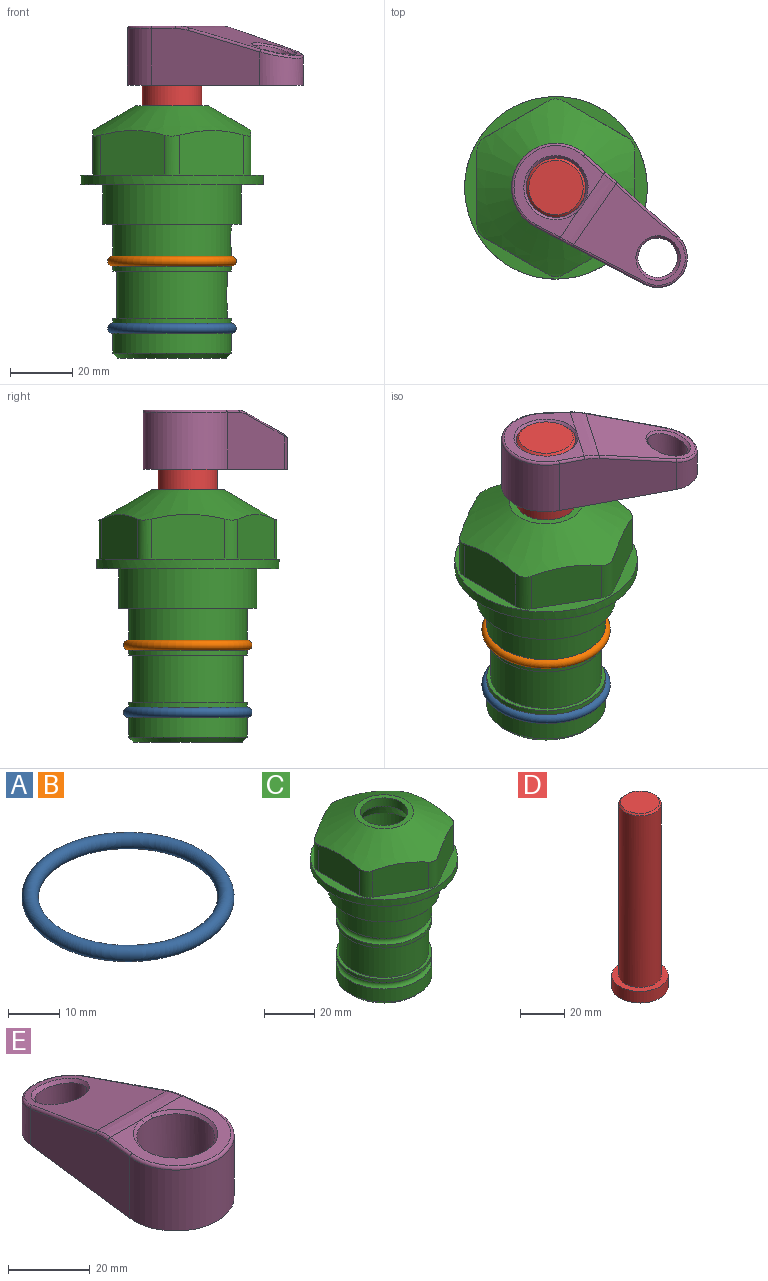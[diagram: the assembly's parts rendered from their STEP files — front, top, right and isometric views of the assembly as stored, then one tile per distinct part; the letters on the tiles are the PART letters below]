
ASSEMBLY  parts=5 mates=4
PART A: 1 faces, bbox 44.7x44.7x3.2 mm
  f0: torus R=19.05mm, axis (0,0,1), area 1193.9mm2
PART B: same geometry as A
PART C: 36 faces, bbox 58.7x58.7x81 mm
  f0: cylinder r=17.78mm len=35.56mm, axis (0,0,1), area 1670.8mm2, adj f23,f24,f31
  f1: cylinder r=19.05mm len=38.1mm, axis (0,0,1), area 1191.9mm2, adj f26,f27,f30
  f2: plane 58.66x58.66mm, normal (0,0,-1), area 1150.6mm2, adj f3,f28
  f3: cylinder r=29.33mm len=58.66mm, axis (0,0,-1), area 585.1mm2, adj f2,f4
  f4: plane 58.66x58.66mm, normal (0,0,1), area 475.9mm2, adj f3,f5,f6,f7,f8,f9,f10,f11
  f5: plane 20.32x14.34mm, normal (-0.5,0.87,0), area 324.4mm2, adj f4,f15,f16,f17
  f6: plane 20.32x14.34mm, normal (0.5,0.87,0), area 324.4mm2, adj f4,f14,f15,f17
  f7: plane 23.48x14.34mm, normal (1,0,0), area 324.4mm2, adj f4,f13,f14,f17
  f8: plane 20.32x14.34mm, normal (0.5,-0.87,0), area 324.4mm2, adj f4,f12,f13,f17
  f9: plane 20.32x14.34mm, normal (-0.5,-0.87,0), area 324.4mm2, adj f4,f11,f12,f17
  f10: plane 23.48x14.34mm, normal (-1,0,0), area 324.4mm2, adj f4,f11,f16,f17
  f11: cylinder r=5.08mm len=12.85mm, axis (0,0,-1), area 67.2mm2, adj f4,f9,f10,f17
  f12: cylinder r=5.08mm len=12.85mm, axis (0,0,-1), area 67.2mm2, adj f4,f8,f9,f17
  f13: cylinder r=5.08mm len=12.85mm, axis (0,0,-1), area 67.2mm2, adj f4,f7,f8,f17
  f14: cylinder r=5.08mm len=12.85mm, axis (0,0,-1), area 67.2mm2, adj f4,f6,f7,f17
  f15: cylinder r=5.08mm len=12.85mm, axis (0,0,-1), area 67.2mm2, adj f4,f5,f6,f17
  f16: cylinder r=5.08mm len=12.85mm, axis (0,0,-1), area 67.2mm2, adj f4,f5,f10,f17
  f17: cone r=11.73mm half-angle=60deg, axis (0,0,-1), area 2071.8mm2, adj f5,f6,f7,f8,f9,f10,f11,f12
  f18: plane 23.46x23.46mm, normal (0,0,1), area 147.4mm2, adj f17,f35
  f19: plane 34.93x34.93mm, normal (0,0,-1), area 958mm2, adj f29
  f20: cylinder r=19.05mm len=38.1mm, axis (0,0,1), area 760.1mm2, adj f21,f29
  f21: torus R=19.05mm, axis (0,0,1), area 565.3mm2, adj f20,f22
  f22: cylinder r=19.05mm len=38.1mm, axis (0,0,1), area 190mm2, adj f21,f23
  f23: plane 38.1x38.1mm, normal (0,0,1), area 146.9mm2, adj f0,f22
  f24: plane 38.1x38.1mm, normal (0,0,-1), area 146.9mm2, adj f0,f25
  f25: cylinder r=19.05mm len=38.1mm, axis (0,0,1), area 190mm2, adj f24,f26
  f26: torus R=19.05mm, axis (0,0,1), area 565.3mm2, adj f1,f25
  f27: plane 44.45x44.45mm, normal (0,0,-1), area 411.7mm2, adj f1,f28
  f28: cylinder r=22.23mm len=44.45mm, axis (0,0,1), area 1773.5mm2, adj f2,f27
  f29: cone r=19.05mm half-angle=45deg, axis (0,0,1), area 257.5mm2, adj f19,f20
  f30: cylinder r=3.17mm len=6.75mm, axis (-1,0,0), area 128mm2, adj f1,f33
  f31: cylinder r=3.17mm len=6.35mm, axis (-1,0,0), area 102.5mm2, adj f0,f33
  f32: plane 25.4x25.4mm, normal (0,0,1), area 506.7mm2, adj f33
  f33: cylinder r=12.7mm len=66.42mm, axis (0,0,-1), area 5236.2mm2, adj f30,f31,f32,f34
  f34: cone r=9.53mm half-angle=30deg, axis (0,0,-1), area 443.4mm2, adj f33,f35
  f35: cylinder r=9.53mm len=19.05mm, axis (0,0,-1), area 240.9mm2, adj f18,f34
PART D: 6 faces, bbox 25.4x25.4x101.6 mm
  f0: plane 17.46x17.46mm, normal (0,0,1), area 239.5mm2, adj f5
  f1: plane 25.4x25.4mm, normal (0,0,-1), area 506.7mm2, adj f2
  f2: cylinder r=12.7mm len=25.4mm, axis (0,0,1), area 506.7mm2, adj f1,f3
  f3: plane 25.4x25.4mm, normal (0,0,1), area 221.7mm2, adj f2,f4
  f4: cylinder r=9.53mm len=94.46mm, axis (0,0,1), area 5653mm2, adj f3,f5
  f5: cone r=8.73mm half-angle=45deg, axis (0,0,-1), area 64.4mm2, adj f0,f4
PART E: 31 faces, bbox 31.7x65.5x19.8 mm
  f0: plane 39.12x18.26mm, normal (0.99,0.12,0), area 612.2mm2, adj f1,f4,f7,f11,f13,f15
  f1: cylinder r=9.53mm len=18.91mm, axis (0,0,-1), area 296.1mm2, adj f0,f2,f7,f17
  f2: plane 39.12x18.26mm, normal (-0.99,0.12,0), area 612.2mm2, adj f1,f4,f7,f12,f14,f16
  f3: cylinder r=6.35mm len=12.7mm, axis (0,0,-1), area 362.4mm2, adj f7,f18
  f4: cylinder r=14.29mm len=28.58mm, axis (0,0,-1), area 882.2mm2, adj f0,f2,f7,f10
  f5: cylinder r=9.53mm len=19.05mm, axis (0,0,-1), area 1092.6mm2, adj f7,f19,f20
  f6: plane 26.99x23.69mm, normal (0,0,1), area 216.2mm2, adj f9,f10,f11,f12,f19
  f7: plane 63.5x28.58mm, normal (0,0,-1), area 661.8mm2, adj f0,f1,f2,f3,f4,f5,f22,f23
  f8: plane 33.52x23.6mm, normal (0,0.26,0.97), area 486mm2, adj f9,f15,f16,f17,f18
  f9: cylinder r=19.05mm len=24.72mm, axis (1,0,0), area 120.4mm2, adj f6,f8,f13,f14,f20
  f10: torus R=13.49mm, axis (0,0,1), area 59mm2, adj f4,f6,f11,f12
  f11: cylinder r=0.79mm len=8.67mm, axis (0.12,-0.99,0), area 10.8mm2, adj f0,f6,f10,f13
  f12: cylinder r=0.79mm len=8.67mm, axis (0.12,0.99,0), area 10.8mm2, adj f2,f6,f10,f14
  f13: bspline ~4.95x1.42mm, area 6.1mm2, adj f0,f9,f11,f15
  f14: bspline ~4.95x1.42mm, area 6.1mm2, adj f2,f9,f12,f16
  f15: cylinder r=0.79mm len=25.95mm, axis (0.12,-0.96,0.26), area 32.9mm2, adj f0,f8,f13,f17
  f16: cylinder r=0.79mm len=25.95mm, axis (0.12,0.96,-0.26), area 32.9mm2, adj f2,f8,f14,f17
  f17: bspline ~18.91x8.38mm, area 30mm2, adj f1,f8,f15,f16
  f18: bspline ~14.29x14.29mm, area 48.3mm2, adj f3,f8
  f19: cone r=9.53mm half-angle=45deg, axis (0,0,1), area 66.5mm2, adj f5,f6,f20
  f20: bspline ~3.22x0.96mm, area 3.5mm2, adj f5,f9,f19
  f21: plane 2.75x2.72mm, normal (0,0,-1), area 2.9mm2, adj f23,f25,f28
  f22: plane 23.05x15.88mm, normal (-0.99,-0.12,0), area 323.6mm2, adj f7,f25,f26,f27,f28,f29
  f23: plane 23.05x15.88mm, normal (0.99,-0.12,0), area 323.6mm2, adj f7,f21,f25,f27,f28,f30
  f24: cylinder r=9.53mm len=10.69mm, axis (0,0,-1), area 114.7mm2, adj f7,f27,f29,f30
  f25: cylinder r=12.7mm len=20.59mm, axis (0,0,-1), area 381.1mm2, adj f7,f21,f22,f23,f26,f28
  f26: plane 2.75x2.72mm, normal (0,0,-1), area 2.9mm2, adj f22,f25,f28
  f27: plane 19.72x18.37mm, normal (0,-0.26,-0.97), area 291.8mm2, adj f22,f23,f24,f28,f29,f30
  f28: cylinder r=15.88mm len=19.92mm, axis (1,0,0), area 54.8mm2, adj f21,f22,f23,f25,f26,f27
  f29: cylinder r=1.59mm len=11mm, axis (0,0,-1), area 34.7mm2, adj f7,f22,f24,f27
  f30: cylinder r=1.59mm len=11mm, axis (0,0,-1), area 34.7mm2, adj f7,f23,f24,f27
PLACE A t=(0,0,-21.59)mm
PLACE B at identity
PLACE C at identity fixed
PLACE D rot(axis=(0,0,-1),124.6deg) t=(0,0,-12.45)mm
PLACE E rot(axis=(0,0,-1),124.6deg) t=(0,0,-12.45)mm
MATE fastened D.f2 <-> E.f4  axis (0,0,1) through (0,0,51.05)mm
MATE cylindrical D.f2 <-> C.f0  axis (0,0,-1) through (0,0,-50.55)mm
MATE fastened B.f0 <-> C.f0  axis (0,0,1) through (0,0,-24.51)mm
MATE fastened A.f0 <-> C.f0  axis (0,0,1) through (0,0,-46.1)mm
